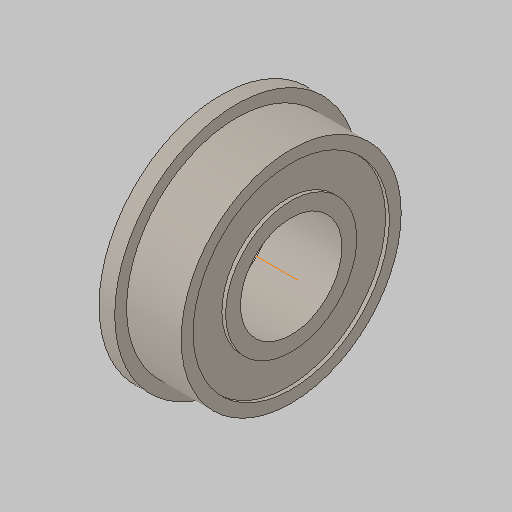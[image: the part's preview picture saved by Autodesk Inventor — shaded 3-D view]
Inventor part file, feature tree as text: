
AUTODESK INVENTOR PART (.ipt)
format: ipt  version: 2023.5 (Build 275446000, 446)  size: 156,672 bytes
history: native  units: in
note: dims shown in document units (in); Inventor stores cm internally (conversion verified against a paired STEP export)
features: revolve x2
ambient origin geometry x8: Origin, YZ Plane, XZ Plane, XY Plane, X Axis, Y Axis, Z Axis, Center Point
bodies: Solid1 (feature_tree)
feature tree (2):
  revolve  "Revolution1"  Angle=90.0deg
  revolve  "Revolve1"  [1 undecoded]
note: 1 required parameter value undecoded (feature->parameter linkage not recoverable at this tier; creation-order binding heuristic only, values carry confidence <= 0.55)
